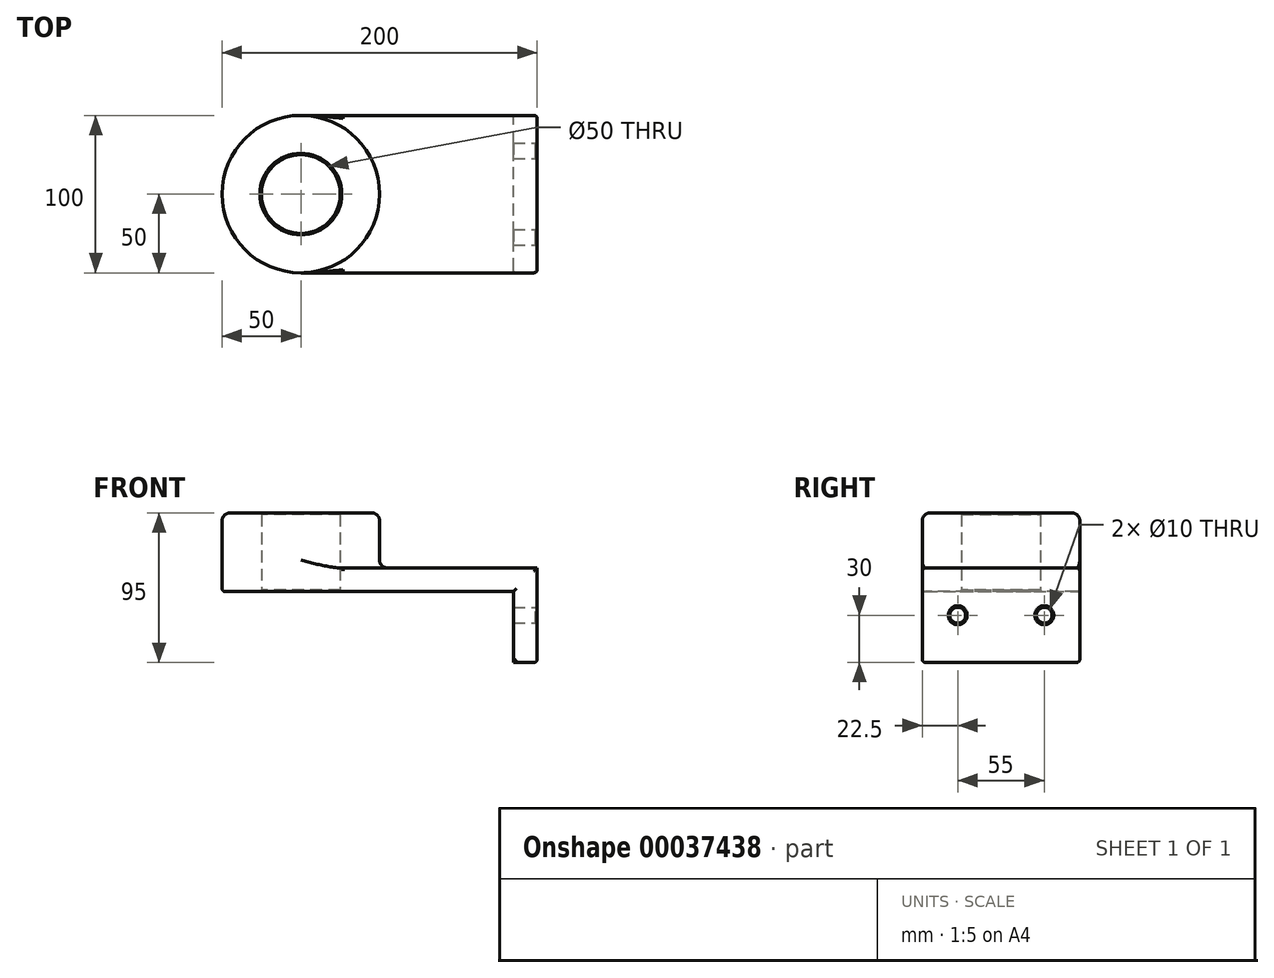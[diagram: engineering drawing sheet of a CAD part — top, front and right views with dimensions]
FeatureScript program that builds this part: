
annotation { "Feature Type Name" : "Feature", "Feature Type Description" : "" }
export const myFeature = defineFeature(function(context is Context, id is Id, definition is map)
    precondition{}
    {
        {
            var Q0;
            Q0=qCreatedBy(makeId("Top.planeOp"),FACE);
            var sketch = newSketch(context, id + "F0", { "sketchPlane" : qUnion([Q0])});
            skLineSegment(sketch, "E0.rect.bottom", {"start": v(-75, 50) * mm, "end": v(75, 50) * mm});
            skLineSegment(sketch, "E0.rect.top", {"start": v(-75, -50) * mm, "end": v(75, -50) * mm});
            skLineSegment(sketch, "E0.rect.left", {"start": v(-75, 50) * mm, "end": v(-75, -50) * mm});
            skLineSegment(sketch, "E0.rect.right", {"start": v(75, 50) * mm, "end": v(75, -50) * mm});
            skPoint(sketch, "E0.rect.middle", {"position": v(0, 0) * mm});
            skCircle(sketch, "E1", {"center": v(-75, 0) * mm, "radius": 50 * mm});
            skCircle(sketch, "E2", {"center": v(-75, 0) * mm, "radius": 25 * mm});
            skSolve(sketch);
        }
        {
            var Q0;
            {var subQ0=sQuery(id+"F0.wireOp",EDGE,"E2");var subQ1=sQuery(id+"F0.wireOp",EDGE,"E0.rect.left");var subQ3=makeQuery(id+"F0.imprint","INTERSECT",VERTEX,{"disambiguationData":[OD(0.0)],"derivedFrom":[subQ1,subQ0]});Q0=makeQuery(id+"F0.imprint","IMPRINT",FACE,{"disambiguationData":[TD([[makeQuery(id+"F0.imprint","IMPRINT",EDGE,{"disambiguationData":[TD([[subQ3,-1.0]])],"derivedFrom":subQ0}),-1.0]])]});}
            var Q1;
            {var subQ0=sQuery(id+"F0.wireOp",EDGE,"E2");var subQ1=sQuery(id+"F0.wireOp",EDGE,"E0.rect.left");var subQ3=makeQuery(id+"F0.imprint","INTERSECT",VERTEX,{"disambiguationData":[OD(0.0)],"derivedFrom":[subQ1,subQ0]});Q1=makeQuery(id+"F0.imprint","IMPRINT",FACE,{"disambiguationData":[TD([[makeQuery(id+"F0.imprint","IMPRINT",EDGE,{"disambiguationData":[TD([[subQ3,1.0]])],"derivedFrom":subQ0}),-1.0]])]});}
            var Q2;
            {var subQ3=sQuery(id+"F0.wireOp",EDGE,"E0.rect.bottom");Q2=makeQuery(id+"F0.imprint","IMPRINT",FACE,{"disambiguationData":[TD([[makeQuery(id+"F0.imprint","IMPRINT",EDGE,{"derivedFrom":subQ3}),-1.0]])]});}
            extrude(context, id + "F1", {"entities" : qUnion([Q0, Q1, Q2]), "depth" : 15 * mm});
        }
        {
            var Q0;
            {var subQ0=sQuery(id+"F0.wireOp",EDGE,"E2");var subQ1=sQuery(id+"F0.wireOp",EDGE,"E0.rect.left");var subQ3=makeQuery(id+"F0.imprint","INTERSECT",VERTEX,{"disambiguationData":[OD(0.0)],"derivedFrom":[subQ1,subQ0]});Q0=makeQuery(id+"F0.imprint","IMPRINT",FACE,{"disambiguationData":[TD([[makeQuery(id+"F0.imprint","IMPRINT",EDGE,{"disambiguationData":[TD([[subQ3,-1.0]])],"derivedFrom":subQ0}),-1.0]])]});}
            var Q1;
            {var subQ0=sQuery(id+"F0.wireOp",EDGE,"E2");var subQ1=sQuery(id+"F0.wireOp",EDGE,"E0.rect.left");var subQ3=makeQuery(id+"F0.imprint","INTERSECT",VERTEX,{"disambiguationData":[OD(0.0)],"derivedFrom":[subQ1,subQ0]});Q1=makeQuery(id+"F0.imprint","IMPRINT",FACE,{"disambiguationData":[TD([[makeQuery(id+"F0.imprint","IMPRINT",EDGE,{"disambiguationData":[TD([[subQ3,1.0]])],"derivedFrom":subQ0}),-1.0]])]});}
            extrude(context, id + "F2", {"entities" : qUnion([Q0, Q1]), "operationType" : NewBodyOperationType.ADD, "depth" : 50 * mm});
        }
        {
            var Q0;
            Q0=makeQuery(id+"F1.opExtrude","SWEPT_FACE",FACE,{"disambiguationData":[OSD([sQuery(id+"F0.wireOp",EDGE,"E0.rect.right")])]});
            var sketch = newSketch(context, id + "F3", { "sketchPlane" : qUnion([Q0])});
            skLineSegment(sketch, "E3.bottom", {"start": v(-50, 15) * mm, "end": v(50, 15) * mm});
            skLineSegment(sketch, "E3.top", {"start": v(-50, -45) * mm, "end": v(50, -45) * mm});
            skLineSegment(sketch, "E3.left", {"start": v(-50, 15) * mm, "end": v(-50, -45) * mm});
            skLineSegment(sketch, "E3.right", {"start": v(50, 15) * mm, "end": v(50, -45) * mm});
            skCircle(sketch, "E4", {"center": v(-27.5, -15) * mm, "radius": 5 * mm});
            skPoint(sketch, "E4.centerSnap0", {"position": v(-50, -15) * mm});
            skLineSegment(sketch, "E5", {"start": v(0, 15) * mm, "end": v(0, -45) * mm, "construction": true});
            skCircle(sketch, "E6.MirrorC", {"center": v(27.5, -15) * mm, "radius": 5 * mm});
            skSolve(sketch);
        }
        {
            var Q0;
            Q0 = qSketchRegion(id + "F3", true);
            extrude(context, id + "F4", {"entities" : qUnion([Q0]), "operationType" : NewBodyOperationType.ADD, "oppositeDirection" : true, "depth" : 15 * mm});
        }
        {
            var Q0;
            {var subQ0=sQuery(id+"F0.wireOp",EDGE,"E1");Q0=makeQuery(id+"F2.boolean.opBoolean","INTERSECT",EDGE,{"derivedFrom":[makeQuery(id+"F1.opExtrude","CAP_FACE",FACE,{"disambiguationData":[OSD([sQuery(id+"F0.wireOp",EDGE,"E0.rect.bottom"),sQuery(id+"F0.wireOp",EDGE,"E0.rect.top"),sQuery(id+"F0.wireOp",EDGE,"E0.rect.right"),subQ0,sQuery(id+"F0.wireOp",EDGE,"E2")])],"isStart":false}),makeQuery(id+"F2.opExtrude","SWEPT_FACE",FACE,{"disambiguationData":[OSD([subQ0])]})]});}
            fillet(context, id + "F5", {"entities" : qUnion([Q0]), "radius" : 5 * mm, "tangentPropagation" : true, "allowEdgeOverflow" : false});
        }
        {
            var Q0;
            Q0=makeQuery(id+"F1.opExtrude","CAP_EDGE",EDGE,{"disambiguationData":[OSD([sQuery(id+"F0.wireOp",EDGE,"E0.rect.top")])],"isStart":false});
            var Q1;
            Q1=makeQuery(id+"F1.opExtrude","CAP_EDGE",EDGE,{"disambiguationData":[OSD([sQuery(id+"F0.wireOp",EDGE,"E0.rect.bottom")])],"isStart":false});
            var Q2;
            Q2=makeQuery(id+"F1.opExtrude","CAP_EDGE",EDGE,{"disambiguationData":[OSD([sQuery(id+"F0.wireOp",EDGE,"E0.rect.bottom")])],"isStart":true});
            var Q3;
            Q3=makeQuery(id+"F4.opExtrude","SWEPT_EDGE",EDGE,{"disambiguationData":[OSD([sQuery(id+"F3.wireOp",EDGE,"E3.top"),sQuery(id+"F3.wireOp",EDGE,"E3.right")])]});
            var Q4;
            Q4=makeQuery(id+"F4.opExtrude","CAP_EDGE",EDGE,{"disambiguationData":[OSD([sQuery(id+"F3.wireOp",EDGE,"E3.right")])],"isStart":false});
            var Q5;
            Q5=makeQuery(id+"F4.boolean.opBoolean","MERGE",EDGE,{"derivedFrom":[makeQuery(id+"F1.opExtrude","SWEPT_EDGE",EDGE,{"disambiguationData":[OSD([sQuery(id+"F0.wireOp",EDGE,"E0.rect.bottom"),sQuery(id+"F0.wireOp",EDGE,"E0.rect.right")])]}),makeQuery(id+"F4.opExtrude","CAP_EDGE",EDGE,{"disambiguationData":[OSD([sQuery(id+"F3.wireOp",EDGE,"E3.right")])],"isStart":true})]});
            var Q6;
            Q6=makeQuery(id+"F4.opExtrude","CAP_EDGE",EDGE,{"disambiguationData":[OSD([sQuery(id+"F3.wireOp",EDGE,"E3.top")])],"isStart":true});
            var Q7;
            Q7=makeQuery(id+"F4.boolean.opBoolean","MERGE",EDGE,{"derivedFrom":[makeQuery(id+"F1.opExtrude","SWEPT_EDGE",EDGE,{"disambiguationData":[OSD([sQuery(id+"F0.wireOp",EDGE,"E0.rect.top"),sQuery(id+"F0.wireOp",EDGE,"E0.rect.right")])]}),makeQuery(id+"F4.opExtrude","CAP_EDGE",EDGE,{"disambiguationData":[OSD([sQuery(id+"F3.wireOp",EDGE,"E3.left")])],"isStart":true})]});
            var Q8;
            Q8=makeQuery(id+"F4.opExtrude","SWEPT_EDGE",EDGE,{"disambiguationData":[OSD([sQuery(id+"F3.wireOp",EDGE,"E3.top"),sQuery(id+"F3.wireOp",EDGE,"E3.left")])]});
            var Q9;
            Q9=makeQuery(id+"F4.opExtrude","CAP_EDGE",EDGE,{"disambiguationData":[OSD([sQuery(id+"F3.wireOp",EDGE,"E3.left")])],"isStart":false});
            var Q10;
            Q10=makeQuery(id+"F1.opExtrude","CAP_EDGE",EDGE,{"disambiguationData":[OSD([sQuery(id+"F0.wireOp",EDGE,"E0.rect.top")])],"isStart":true});
            fillet(context, id + "F6", {"entities" : qUnion([Q0, Q1, Q2, Q3, Q4, Q5, Q6, Q7, Q8, Q9, Q10]), "radius" : 2 * mm, "tangentPropagation" : true, "allowEdgeOverflow" : false});
        }
        {
            var Q0;
            Q0=makeQuery(id+"F2.opExtrude","CAP_EDGE",EDGE,{"disambiguationData":[OSD([sQuery(id+"F0.wireOp",EDGE,"E2")])],"isStart":false});
            var Q1;
            Q1=makeQuery(id+"F4.opExtrude","CAP_EDGE",EDGE,{"disambiguationData":[OSD([sQuery(id+"F3.wireOp",EDGE,"E4")])],"isStart":true});
            var Q2;
            Q2=makeQuery(id+"F4.opExtrude","CAP_EDGE",EDGE,{"disambiguationData":[OSD([sQuery(id+"F3.wireOp",EDGE,"E6.MirrorC")])],"isStart":true});
            var Q3;
            Q3=makeQuery(id+"F1.opExtrude","CAP_EDGE",EDGE,{"disambiguationData":[OSD([sQuery(id+"F0.wireOp",EDGE,"E2")])],"isStart":true});
            chamfer(context, id + "F7", {"entities" : qUnion([Q0, Q1, Q2, Q3]), "width" : 1 * mm, "tangentPropagation" : true});
        }
        {
            var Q0;
            Q0=makeQuery(id+"F2.opExtrude","CAP_EDGE",EDGE,{"disambiguationData":[OSD([sQuery(id+"F0.wireOp",EDGE,"E1")])],"isStart":false});
            fillet(context, id + "F8", {"entities" : qUnion([Q0]), "radius" : 5 * mm, "tangentPropagation" : true, "allowEdgeOverflow" : false});
        }
    });
